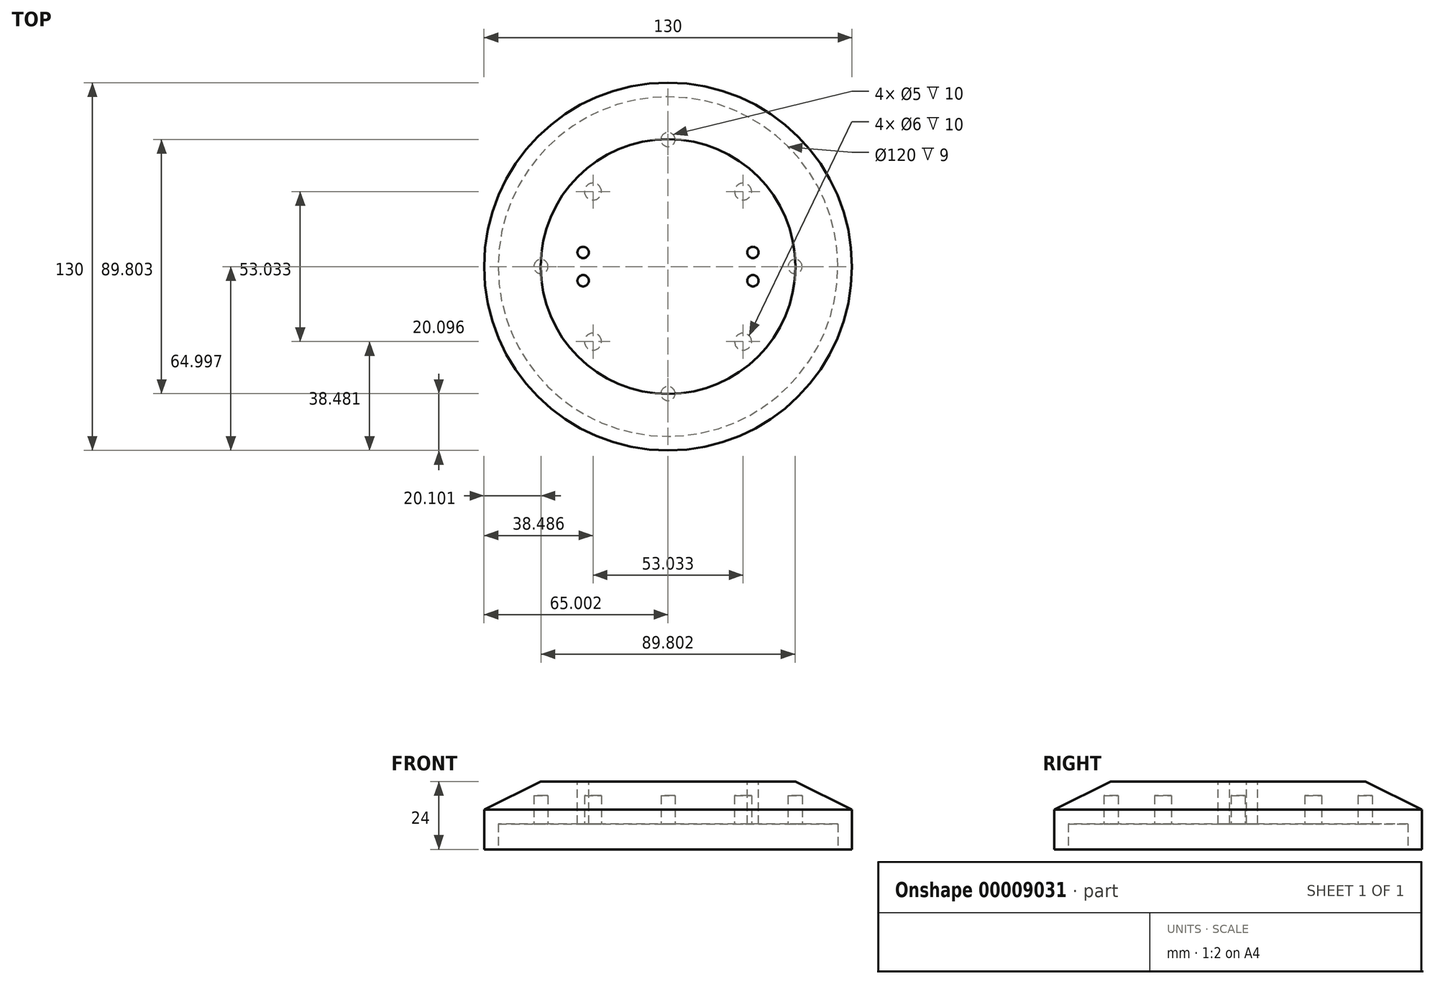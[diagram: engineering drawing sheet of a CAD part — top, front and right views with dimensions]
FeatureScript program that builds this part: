
annotation { "Feature Type Name" : "Feature", "Feature Type Description" : "" }
export const myFeature = defineFeature(function(context is Context, id is Id, definition is map)
    precondition{}
    {
        {
            var Q0;
            Q0=qCreatedBy(makeId("Top.planeOp"),FACE);
            var sketch = newSketch(context, id + "F0", { "sketchPlane" : qUnion([Q0])});
            skCircle(sketch, "E0", {"center": v(-5.76, 12.5) * mm, "radius": 60 * mm});
            skLineSegment(sketch, "E1.rect.bottom", {"start": v(-37.51, -25.6) * mm, "end": v(25.99, -25.6) * mm, "construction": true});
            skLineSegment(sketch, "E1.rect.top", {"start": v(-37.51, 50.6) * mm, "end": v(25.99, 50.6) * mm, "construction": true});
            skLineSegment(sketch, "E1.rect.left", {"start": v(-43.86, -19.26) * mm, "end": v(-43.86, 44.24) * mm, "construction": true});
            skLineSegment(sketch, "E1.rect.right", {"start": v(32.34, -19.26) * mm, "end": v(32.34, 44.24) * mm, "construction": true});
            skPoint(sketch, "E2.visualSharp", {"position": v(-43.86, 50.6) * mm});
            skArc(sketch, "E2.filletArc", {"start": v(-37.51, 50.6) * mm, "mid": v(-42, 48.73) * mm, "end": v(-43.86, 44.24) * mm, "construction": true});
            skPoint(sketch, "E3.visualSharp", {"position": v(-43.86, -25.6) * mm});
            skArc(sketch, "E3.filletArc", {"start": v(-43.86, -19.26) * mm, "mid": v(-42, -23.75) * mm, "end": v(-37.51, -25.6) * mm, "construction": true});
            skPoint(sketch, "E4.visualSharp", {"position": v(32.34, -25.6) * mm});
            skArc(sketch, "E4.filletArc", {"start": v(25.99, -25.6) * mm, "mid": v(30.48, -23.75) * mm, "end": v(32.34, -19.26) * mm, "construction": true});
            skPoint(sketch, "E5.visualSharp", {"position": v(32.34, 50.6) * mm});
            skArc(sketch, "E5.filletArc", {"start": v(32.34, 44.24) * mm, "mid": v(30.48, 48.73) * mm, "end": v(25.99, 50.6) * mm, "construction": true});
            skArc(sketch, "E6", {"start": v(-43.86, 50.6) * mm, "mid": v(-18.4, -6.27) * mm, "end": v(40.99, -25.12) * mm, "construction": true});
            skCircle(sketch, "E7", {"center": v(-37.51, 44.24) * mm, "radius": 2.5 * mm});
            skCircle(sketch, "E8", {"center": v(25.99, 44.24) * mm, "radius": 2.5 * mm});
            skCircle(sketch, "E9", {"center": v(25.99, -19.26) * mm, "radius": 2.5 * mm});
            skCircle(sketch, "E10", {"center": v(-37.51, -19.26) * mm, "radius": 2.5 * mm});
            skCircle(sketch, "E11", {"center": v(-5.76, 12.5) * mm, "radius": 30 * mm, "construction": true});
            skCircle(sketch, "E12", {"center": v(-5.76, 12.5) * mm, "radius": 45 * mm, "construction": true});
            skCircle(sketch, "E13", {"center": v(-5.76, 50) * mm, "radius": 3 * mm});
            skLineSegment(sketch, "E14", {"start": v(-5.76, -17.5) * mm, "end": v(-5.76, -32.5) * mm, "construction": true});
            skLineSegment(sketch, "E15", {"start": v(-5.76, 42.5) * mm, "end": v(-5.76, 57.5) * mm, "construction": true});
            skLineSegment(sketch, "E16", {"start": v(-35.76, 12.5) * mm, "end": v(-50.76, 12.5) * mm, "construction": true});
            skLineSegment(sketch, "E17", {"start": v(24.24, 12.5) * mm, "end": v(39.24, 12.5) * mm, "construction": true});
            skCircle(sketch, "E18", {"center": v(31.74, 12.5) * mm, "radius": 3 * mm});
            skCircle(sketch, "E19", {"center": v(-5.76, -25) * mm, "radius": 3 * mm});
            skCircle(sketch, "E20", {"center": v(-43.26, 12.5) * mm, "radius": 3 * mm});
            skCircle(sketch, "E21", {"center": v(-5.76, 12.5) * mm, "radius": 65 * mm});
            skSolve(sketch);
        }
        {
            var Q0;
            Q0=makeQuery(id+"F0.imprint","IMPRINT",FACE,{"disambiguationData":[TD([[makeQuery(id+"F0.imprint","IMPRINT",EDGE,{"derivedFrom":sQuery(id+"F0.wireOp",EDGE,"E0")}),-1.0]])]});
            var Q1;
            Q1=makeQuery(id+"F0.imprint","IMPRINT",FACE,{"disambiguationData":[TD([[makeQuery(id+"F0.imprint","IMPRINT",EDGE,{"derivedFrom":sQuery(id+"F0.wireOp",EDGE,"E7")}),1.0]])]});
            var Q2;
            Q2=makeQuery(id+"F0.imprint","IMPRINT",FACE,{"disambiguationData":[TD([[makeQuery(id+"F0.imprint","IMPRINT",EDGE,{"derivedFrom":sQuery(id+"F0.wireOp",EDGE,"E13")}),1.0]])]});
            var Q3;
            Q3=makeQuery(id+"F0.imprint","IMPRINT",FACE,{"disambiguationData":[TD([[makeQuery(id+"F0.imprint","IMPRINT",EDGE,{"derivedFrom":sQuery(id+"F0.wireOp",EDGE,"E8")}),1.0]])]});
            var Q4;
            Q4=makeQuery(id+"F0.imprint","IMPRINT",FACE,{"disambiguationData":[TD([[makeQuery(id+"F0.imprint","IMPRINT",EDGE,{"derivedFrom":sQuery(id+"F0.wireOp",EDGE,"E18")}),1.0]])]});
            var Q5;
            Q5=makeQuery(id+"F0.imprint","IMPRINT",FACE,{"disambiguationData":[TD([[makeQuery(id+"F0.imprint","IMPRINT",EDGE,{"derivedFrom":sQuery(id+"F0.wireOp",EDGE,"E9")}),1.0]])]});
            var Q6;
            Q6=makeQuery(id+"F0.imprint","IMPRINT",FACE,{"disambiguationData":[TD([[makeQuery(id+"F0.imprint","IMPRINT",EDGE,{"derivedFrom":sQuery(id+"F0.wireOp",EDGE,"E19")}),1.0]])]});
            var Q7;
            Q7=makeQuery(id+"F0.imprint","IMPRINT",FACE,{"disambiguationData":[TD([[makeQuery(id+"F0.imprint","IMPRINT",EDGE,{"derivedFrom":sQuery(id+"F0.wireOp",EDGE,"E10")}),1.0]])]});
            var Q8;
            Q8=makeQuery(id+"F0.imprint","IMPRINT",FACE,{"disambiguationData":[TD([[makeQuery(id+"F0.imprint","IMPRINT",EDGE,{"derivedFrom":sQuery(id+"F0.wireOp",EDGE,"E20")}),1.0]])]});
            var Q9;
            Q9=makeQuery(id+"F0.imprint","IMPRINT",FACE,{"disambiguationData":[TD([[makeQuery(id+"F0.imprint","IMPRINT",EDGE,{"derivedFrom":sQuery(id+"F0.wireOp",EDGE,"E0")}),1.0]])]});
            extrude(context, id + "F1", {"entities" : qUnion([Q0, Q1, Q2, Q3, Q4, Q5, Q6, Q7, Q8, Q9]), "depth" : 24 * mm});
        }
        {
            var Q0;
            Q0=makeQuery(id+"F0.imprint","IMPRINT",FACE,{"disambiguationData":[TD([[makeQuery(id+"F0.imprint","IMPRINT",EDGE,{"derivedFrom":sQuery(id+"F0.wireOp",EDGE,"E10")}),1.0]])]});
            var Q1;
            Q1=makeQuery(id+"F0.imprint","IMPRINT",FACE,{"disambiguationData":[TD([[makeQuery(id+"F0.imprint","IMPRINT",EDGE,{"derivedFrom":sQuery(id+"F0.wireOp",EDGE,"E19")}),1.0]])]});
            var Q2;
            Q2=makeQuery(id+"F0.imprint","IMPRINT",FACE,{"disambiguationData":[TD([[makeQuery(id+"F0.imprint","IMPRINT",EDGE,{"derivedFrom":sQuery(id+"F0.wireOp",EDGE,"E9")}),1.0]])]});
            var Q3;
            Q3=makeQuery(id+"F0.imprint","IMPRINT",FACE,{"disambiguationData":[TD([[makeQuery(id+"F0.imprint","IMPRINT",EDGE,{"derivedFrom":sQuery(id+"F0.wireOp",EDGE,"E18")}),1.0]])]});
            var Q4;
            Q4=makeQuery(id+"F0.imprint","IMPRINT",FACE,{"disambiguationData":[TD([[makeQuery(id+"F0.imprint","IMPRINT",EDGE,{"derivedFrom":sQuery(id+"F0.wireOp",EDGE,"E8")}),1.0]])]});
            var Q5;
            Q5=makeQuery(id+"F0.imprint","IMPRINT",FACE,{"disambiguationData":[TD([[makeQuery(id+"F0.imprint","IMPRINT",EDGE,{"derivedFrom":sQuery(id+"F0.wireOp",EDGE,"E13")}),1.0]])]});
            var Q6;
            Q6=makeQuery(id+"F0.imprint","IMPRINT",FACE,{"disambiguationData":[TD([[makeQuery(id+"F0.imprint","IMPRINT",EDGE,{"derivedFrom":sQuery(id+"F0.wireOp",EDGE,"E7")}),1.0]])]});
            var Q7;
            Q7=makeQuery(id+"F0.imprint","IMPRINT",FACE,{"disambiguationData":[TD([[makeQuery(id+"F0.imprint","IMPRINT",EDGE,{"derivedFrom":sQuery(id+"F0.wireOp",EDGE,"E20")}),1.0]])]});
            extrude(context, id + "F2", {"entities" : qUnion([Q0, Q1, Q2, Q3, Q4, Q5, Q6, Q7]), "operationType" : NewBodyOperationType.REMOVE, "depth" : 19 * mm});
        }
        {
            var Q0;
            Q0=makeQuery(id+"F0.imprint","IMPRINT",FACE,{"disambiguationData":[TD([[makeQuery(id+"F0.imprint","IMPRINT",EDGE,{"derivedFrom":sQuery(id+"F0.wireOp",EDGE,"E0")}),1.0]])]});
            extrude(context, id + "F3", {"entities" : qUnion([Q0]), "operationType" : NewBodyOperationType.REMOVE, "depth" : 9 * mm});
        }
        {
            var Q0;
            Q0=makeQuery(id+"F1.opExtrude","CAP_EDGE",EDGE,{"disambiguationData":[OSD([sQuery(id+"F0.wireOp",EDGE,"E21")])],"isStart":false});
            chamfer(context, id + "F4", {"entities" : qUnion([Q0]), "chamferType" : ChamferType.TWO_OFFSETS, "width1" : 20 * mm, "oppositeDirection" : false, "width2" : 10 * mm, "tangentPropagation" : true});
        }
        {
            var Q0;
            Q0=makeQuery(id+"F1.opExtrude","SWEPT_BODY",BODY,{"disambiguationData":[OSD([sQuery(id+"F0.wireOp",EDGE,"E21")])]});
            var Q1;
            Q1=makeQuery(id+"F2.boolean.opBoolean","COPY",FACE,{"derivedFrom":makeQuery(id+"F2.opExtrude","SWEPT_FACE",FACE,{"disambiguationData":[OSD([sQuery(id+"F0.wireOp",EDGE,"E20")])]})});
            transform(context, id + "F5", {"entities" : qUnion([Q0]), "transformType" : TransformType.ROTATION, "transformAxis" : qUnion([Q1]), "angle" : 45 * degree, "makeCopy" : false});
        }
        {
            var Q0;
            Q0=makeQuery(id+"F1.opExtrude","CAP_FACE",FACE,{"disambiguationData":[OSD([sQuery(id+"F0.wireOp",EDGE,"E21")])],"isStart":false});
            var sketch = newSketch(context, id + "F6", { "sketchPlane" : qUnion([Q0])});
            skCircle(sketch, "E22.0.0", {"center": v(-16.75, 39) * mm, "radius": 45 * mm});
            skLineSegment(sketch, "E23.rect.bottom", {"start": v(17.25, 30) * mm, "end": v(-50.75, 30) * mm});
            skLineSegment(sketch, "E23.rect.top", {"start": v(17.25, 48) * mm, "end": v(-50.75, 48) * mm});
            skLineSegment(sketch, "E23.rect.left", {"start": v(17.25, 30) * mm, "end": v(17.25, 48) * mm});
            skLineSegment(sketch, "E23.rect.right", {"start": v(-50.75, 30) * mm, "end": v(-50.75, 48) * mm});
            skLineSegment(sketch, "E24", {"start": v(-50.75, 44) * mm, "end": v(-46.75, 44) * mm, "construction": true});
            skLineSegment(sketch, "E25", {"start": v(-46.75, 44) * mm, "end": v(-46.75, 48) * mm, "construction": true});
            skLineSegment(sketch, "E26", {"start": v(-46.75, 30) * mm, "end": v(-46.75, 34) * mm, "construction": true});
            skLineSegment(sketch, "E27", {"start": v(17.25, 44) * mm, "end": v(13.25, 44) * mm, "construction": true});
            skCircle(sketch, "E28", {"center": v(-46.75, 44) * mm, "radius": 2 * mm});
            skCircle(sketch, "E29", {"center": v(13.25, 44) * mm, "radius": 2 * mm});
            skCircle(sketch, "E30", {"center": v(-46.75, 34) * mm, "radius": 2 * mm});
            skCircle(sketch, "E31", {"center": v(13.25, 34) * mm, "radius": 2 * mm});
            skSolve(sketch);
        }
        {
            var Q0;
            Q0=makeQuery(id+"F6.imprint","IMPRINT",FACE,{"disambiguationData":[TD([[makeQuery(id+"F6.imprint","IMPRINT",EDGE,{"derivedFrom":sQuery(id+"F6.wireOp",EDGE,"E30")}),1.0]])]});
            var Q1;
            Q1=makeQuery(id+"F6.imprint","IMPRINT",FACE,{"disambiguationData":[TD([[makeQuery(id+"F6.imprint","IMPRINT",EDGE,{"derivedFrom":sQuery(id+"F6.wireOp",EDGE,"E28")}),1.0]])]});
            var Q2;
            Q2=makeQuery(id+"F6.imprint","IMPRINT",FACE,{"disambiguationData":[TD([[makeQuery(id+"F6.imprint","IMPRINT",EDGE,{"derivedFrom":sQuery(id+"F6.wireOp",EDGE,"E29")}),1.0]])]});
            var Q3;
            Q3=makeQuery(id+"F6.imprint","IMPRINT",FACE,{"disambiguationData":[TD([[makeQuery(id+"F6.imprint","IMPRINT",EDGE,{"derivedFrom":sQuery(id+"F6.wireOp",EDGE,"E31")}),1.0]])]});
            extrude(context, id + "F7", {"entities" : qUnion([Q0, Q1, Q2, Q3]), "operationType" : NewBodyOperationType.REMOVE, "oppositeDirection" : true, "depth" : 25 * mm});
        }
    });
